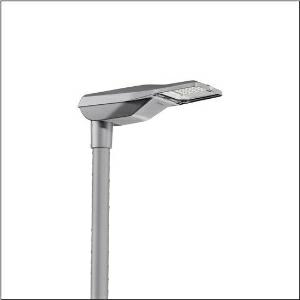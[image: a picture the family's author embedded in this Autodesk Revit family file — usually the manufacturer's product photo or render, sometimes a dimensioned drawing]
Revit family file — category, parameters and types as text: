
# Revit family: streetlight_sl_21_iq_micro___p0_8ab_5xe1r31g08cb_4e53
name_source: partatom
category: Lighting Fixtures
units: mm (PartAtom-declared; Revit-internal decimal feet)

## family parameters
Cut with Voids When Loaded = No
Host = Face
Light Source = No
Part Type = Normal
Room Calculation Point = No
Round Connector Dimension = Use Diameter
Shared = No

## types (1)
- --- (1 x LED, 2510 lm, 19.4 W, 3000K)
    Apparent Load = 19 VA
    CIE Flux Codes = 36 71 98 100 100
    Color Rendering = 70
    Color Temperature = 3000K
    Default Elevation = 1800 mm
    Description = Streetlight SL 21 iQ micro, mast luminaire, primary light control with lens, of PMMA, primary optical cover: cover, of toughened safety glass, transparent, light distribution: P0.8aB, light emission: direct distribution, primary light characteristic: asymmetric, installation type: post-top, side-entry, LED, High Power LED, rated luminous flux: 2.510lm, luminous efficacy: 129lm/W, light colour: 730, colour temperature: 3000K, control gear: iQ Street-Remote, control: pre-setting: linear dimming characteristic, Street-Remote, Auto-Match, Temp-Guard, Lumen-Switch, Night-Set, Smart-Wire, Light-Fading, Desk-Remote (wireless, voltage-free reading and setting of iQ features in the workshop via application-optimized NFC function/RFID function), optimised constant luminous flux control (CLO 2.0), mains connection: 220..240V, AC, 50/60Hz, start of lifetime: 19W, end of service life: 20W, reduction: 10W, luminaire housing, of diecast aluminium, powder-coated, Siteco® metallic grey (DB 702S), corrosivity category C5 mid according to DIN EN ISO 12944, please order mast flange separately, inclination adjustable: 0°, 5°, 10°, 15°, sealing non-destructively replaceable, multi-level sealing system, length: 528mm, width: 235mm, height: 110mm, mast flange for spigot size: 42mm (side-entry): 5XC10008XM4, 60/48mm (side-entry/post-top): 5XC10108XM2, 76/60mm (side-entry/post-top): 5XC10108XM1, protection rating (complete): IP66, insulation class (complete): insulation class II (safety insulation), certification: CE, ENEC, ENEC+, VDE, impact resistance: IK09, permissible operating ambient temperature for outdoor applications: -40..+50°C, standard-compliant lighting for roads and squares, packaging unit: 1 piece

Light Distribution: P0.8aB
    Height = 110 mm
    Lamp = 1 x LED
    Lamp Light Flux = 2510 lm
    Lamp Power = 19.4 W
    Lamp count = 1
    Length = 528 mm
    Luminous efficacy = 129 lm/W
    Manufacturer = Siteco
    ModVariant = No
    Model = 5XE1R31G08CB
    Number of Poles = 1
    OnlyDefault = Yes
    Power Factor = 1
    Product Name = Streetlight SL 21 iQ micro | P0.8aB
    Product group = mast luminaire | pylon top
    ProductGroupID = 6100
    Protection Class = Protection class II
    Protection Degree = IP 66
    RLX_Detail_Level = 1
    RLX_Emergency_Light_Flux = 0 lm
    RLX_Emergency_Type = 0
    RLX_Emergency_Type_DB = No
    RlxData = <blob elided: 99445 chars, md5=cfb50dc2>
    Socket = socket
    Standby Power = 0 W
    System Light Flux = 2510 lm
    System Power = 19 W
    Type Comments = factory setting: luminous flux: 100 % | dim-lin: 254 | 387 mA
    Type Image = l_1006881.jpg
    URL = http://relux.com
    VarID = @adj_071718
    Voltage = 0 V
    Weight = 0.00 kg
    Width = 235 mm

## geometry (parser evidence)
native form markers: Blend x4, Sweep x10
no freeform markers — native parametric forms only
